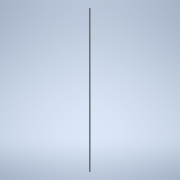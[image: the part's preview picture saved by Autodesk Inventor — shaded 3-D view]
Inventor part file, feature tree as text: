
AUTODESK INVENTOR PART (.ipt)
format: ipt  version: 2022 (Build 260153000, 153)  size: 148,992 bytes
history: native  units: mm
features: extrude x1, sketch x1
ambient origin geometry x8: Origin, YZ Plane, XZ Plane, XY Plane, X Axis, Y Axis, Z Axis, Center Point
bodies: Body1 (feature_tree)
feature tree (2):
  extrude  "Extrusion7"  Depth=5.0mm
  sketch  "Sketch4"  dims[d31=34.456mm d103=5.0mm d104=5.0mm d105=1459.0mm d106=0.0mm]
